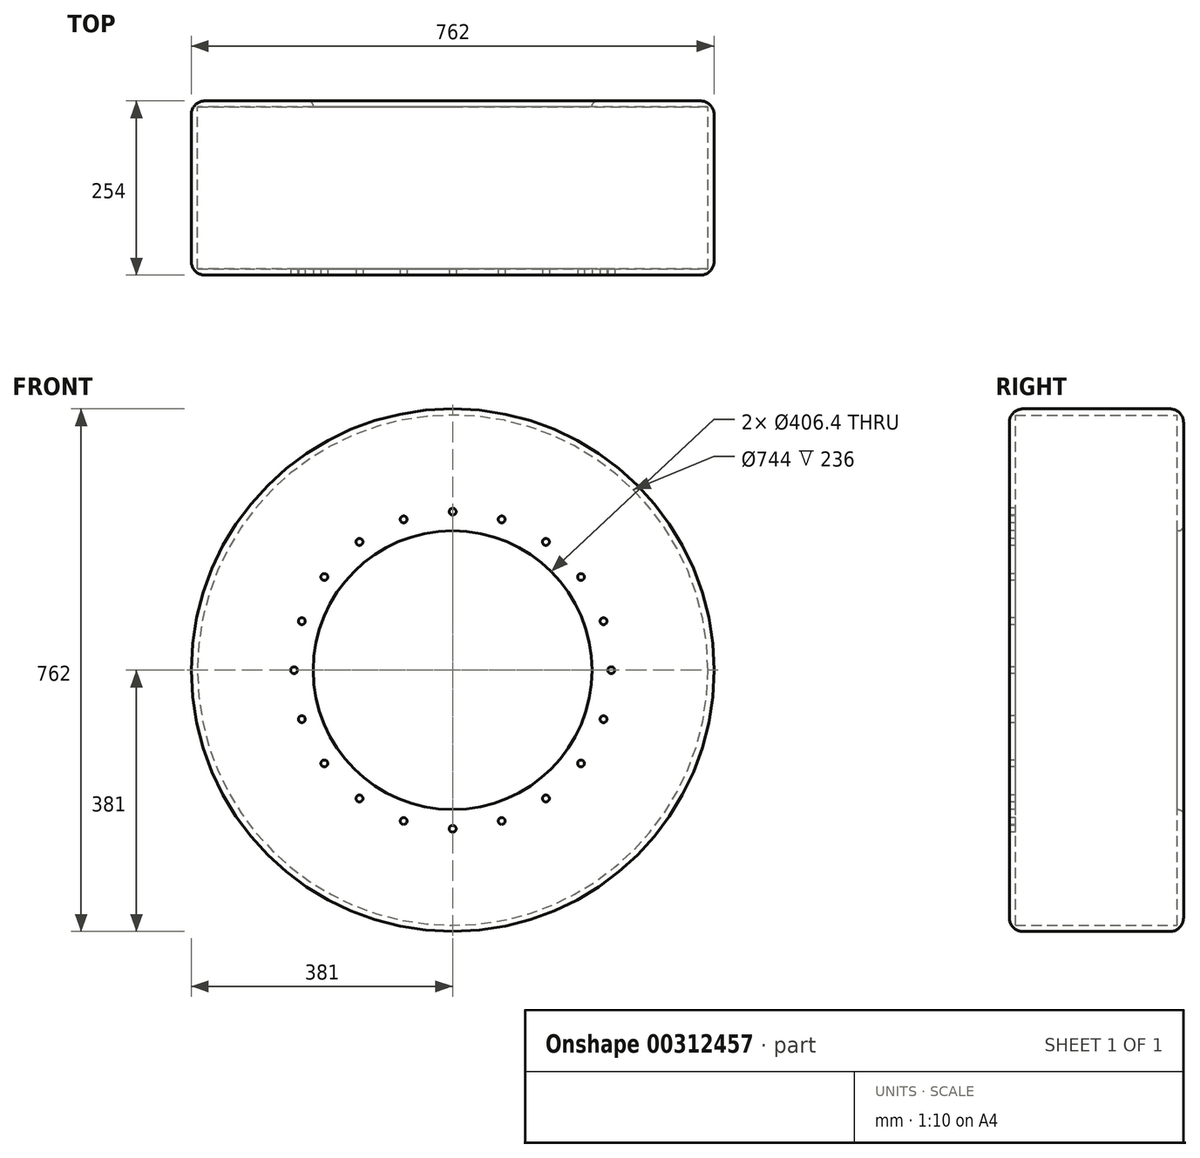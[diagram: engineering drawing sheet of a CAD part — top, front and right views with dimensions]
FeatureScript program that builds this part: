
annotation { "Feature Type Name" : "Feature", "Feature Type Description" : "" }
export const myFeature = defineFeature(function(context is Context, id is Id, definition is map)
    precondition{}
    {
        {
            var Q0;
            Q0=qCreatedBy(makeId("Front.planeOp"),FACE);
            var sketch = newSketch(context, id + "F0", { "sketchPlane" : qUnion([Q0])});
            skCircle(sketch, "E0", {"center": v(0, 0) * mm, "radius": 381 * mm});
            skSolve(sketch);
        }
        {
            var Q0;
            Q0=makeQuery(id+"F0.imprint","IMPRINT",FACE,{"disambiguationData":[TD([[makeQuery(id+"F0.imprint","IMPRINT",EDGE,{"derivedFrom":sQuery(id+"F0.wireOp",EDGE,"E0")}),1.0]])]});
            extrude(context, id + "F1", {"entities" : qUnion([Q0]), "depth" : 254 * mm});
        }
        {
            var Q0;
            Q0=makeQuery(id+"F1.opExtrude","CAP_FACE",FACE,{"disambiguationData":[OSD([sQuery(id+"F0.wireOp",EDGE,"E0")])],"isStart":false});
            var sketch = newSketch(context, id + "F2", { "sketchPlane" : qUnion([Q0])});
            skCircle(sketch, "E1", {"center": v(0, 0) * mm, "radius": 203.2 * mm});
            skSolve(sketch);
        }
        {
            var Q0;
            Q0=makeQuery(id+"F2.imprint","IMPRINT",FACE,{"disambiguationData":[TD([[makeQuery(id+"F2.imprint","IMPRINT",EDGE,{"derivedFrom":sQuery(id+"F2.wireOp",EDGE,"E1")}),1.0]])]});
            extrude(context, id + "F3", {"entities" : qUnion([Q0]), "operationType" : NewBodyOperationType.REMOVE, "oppositeDirection" : true, "depth" : 271.78 * mm});
        }
        {
            var Q0;
            Q0=makeQuery(id+"F3.boolean.opBoolean","COPY",FACE,{"derivedFrom":makeQuery(id+"F3.opExtrude","SWEPT_FACE",FACE,{"disambiguationData":[OSD([sQuery(id+"F2.wireOp",EDGE,"E1")])]})});
            var Q1;
            Q1=makeQuery(id+"F1.opExtrude","SWEPT_BODY",BODY,{"disambiguationData":[OSD([sQuery(id+"F0.wireOp",EDGE,"E0")])]});
            shell(context, id + "F4", {"entities" : qUnion([Q0]), "parts" : qUnion([Q1]), "thickness" : 9 * mm});
        }
        {
            var Q0;
            Q0=makeQuery(id+"F1.opExtrude","CAP_EDGE",EDGE,{"disambiguationData":[OSD([sQuery(id+"F0.wireOp",EDGE,"E0")])],"isStart":false});
            var Q1;
            Q1=makeQuery(id+"F1.opExtrude","CAP_EDGE",EDGE,{"disambiguationData":[OSD([sQuery(id+"F0.wireOp",EDGE,"E0")])],"isStart":true});
            fillet(context, id + "F5", {"entities" : qUnion([Q0, Q1]), "radius" : 20 * mm, "tangentPropagation" : true, "allowEdgeOverflow" : false});
        }
        {
            var Q0;
            Q0=makeQuery(id+"F3.boolean.opBoolean","COPY",EDGE,{"derivedFrom":makeQuery(id+"F3.opExtrude","CAP_EDGE",EDGE,{"disambiguationData":[OSD([sQuery(id+"F2.wireOp",EDGE,"E1")])],"isStart":true})});
            var Q1;
            Q1=makeQuery(id+"F3.boolean.opBoolean","INTERSECT",EDGE,{"derivedFrom":[makeQuery(id+"F1.opExtrude","CAP_FACE",FACE,{"disambiguationData":[OSD([sQuery(id+"F0.wireOp",EDGE,"E0")])],"isStart":true}),makeQuery(id+"F3.opExtrude","SWEPT_FACE",FACE,{"disambiguationData":[OSD([sQuery(id+"F2.wireOp",EDGE,"E1")])]})]});
            fillet(context, id + "F6", {"entities" : qUnion([Q0, Q1]), "radius" : 8 * mm, "tangentPropagation" : true, "allowEdgeOverflow" : false});
        }
        {
            var Q0;
            Q0=makeQuery(id+"F1.opExtrude","CAP_FACE",FACE,{"disambiguationData":[OSD([sQuery(id+"F0.wireOp",EDGE,"E0")])],"isStart":false});
            var sketch = newSketch(context, id + "F7", { "sketchPlane" : qUnion([Q0])});
            skCircle(sketch, "E2", {"center": v(0, 231.2) * mm, "radius": 5 * mm});
            skCircle(sketch, "E3.1.0", {"center": v(-71.44, 219.88) * mm, "radius": 5 * mm});
            skCircle(sketch, "E3.2.0", {"center": v(-135.9, 187.04) * mm, "radius": 5 * mm});
            skCircle(sketch, "E3.3.0", {"center": v(-187.04, 135.9) * mm, "radius": 5 * mm});
            skCircle(sketch, "E3.4.0", {"center": v(-219.88, 71.44) * mm, "radius": 5 * mm});
            skCircle(sketch, "E3.5.0", {"center": v(-231.2, 0) * mm, "radius": 5 * mm});
            skCircle(sketch, "E3.6.0", {"center": v(-219.88, -71.44) * mm, "radius": 5 * mm});
            skCircle(sketch, "E3.7.0", {"center": v(-187.04, -135.9) * mm, "radius": 5 * mm});
            skCircle(sketch, "E3.8.0", {"center": v(-135.9, -187.04) * mm, "radius": 5 * mm});
            skCircle(sketch, "E3.9.0", {"center": v(-71.44, -219.88) * mm, "radius": 5 * mm});
            skCircle(sketch, "E3.10.0", {"center": v(0, -231.2) * mm, "radius": 5 * mm});
            skCircle(sketch, "E3.11.0", {"center": v(71.44, -219.88) * mm, "radius": 5 * mm});
            skCircle(sketch, "E3.12.0", {"center": v(135.9, -187.04) * mm, "radius": 5 * mm});
            skCircle(sketch, "E3.13.0", {"center": v(187.04, -135.9) * mm, "radius": 5 * mm});
            skCircle(sketch, "E3.14.0", {"center": v(219.88, -71.44) * mm, "radius": 5 * mm});
            skCircle(sketch, "E3.15.0", {"center": v(231.2, 0) * mm, "radius": 5 * mm});
            skCircle(sketch, "E3.16.0", {"center": v(219.88, 71.44) * mm, "radius": 5 * mm});
            skCircle(sketch, "E3.17.0", {"center": v(187.04, 135.9) * mm, "radius": 5 * mm});
            skCircle(sketch, "E3.18.0", {"center": v(135.9, 187.04) * mm, "radius": 5 * mm});
            skCircle(sketch, "E3.19.0", {"center": v(71.44, 219.88) * mm, "radius": 5 * mm});
            skPoint(sketch, "E3.center", {"position": v(0, 0) * mm});
            skSolve(sketch);
        }
        {
            var Q0;
            Q0 = qSketchRegion(id + "F7", true);
            extrude(context, id + "F8", {"entities" : qUnion([Q0]), "operationType" : NewBodyOperationType.REMOVE, "endBound" : BoundingType.UP_TO_NEXT, "oppositeDirection" : true, "depth" : 25 * mm});
        }
    });
